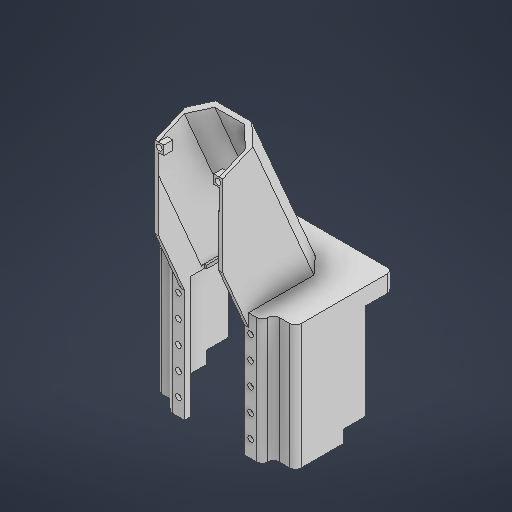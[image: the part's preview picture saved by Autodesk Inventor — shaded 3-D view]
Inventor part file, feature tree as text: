
AUTODESK INVENTOR PART (.ipt)
format: ipt  version: 2025 (Build 290162000, 162)  size: 475,136 bytes
history: native  units: in
note: dims shown in document units (in); Inventor stores cm internally (conversion verified against a paired STEP export)
features: extrude x10, sketch x10, chamfer x2, fillet x1, plane x1
ambient origin geometry x8: Origin, YZ Plane, XZ Plane, XY Plane, X Axis, Y Axis, Z Axis, Center Point
bodies: Solid1 (feature_tree)
feature tree (24):
  extrude  "Extrusion1"  Depth=0.1181in
  extrude  "Extrusion2"  Depth=0.0787in
  extrude  "Extrusion3"  Depth=1.9685in
  fillet  "Fillet1"  Radius=0.9843in
  chamfer  "Chamfer1"  Distance=0.4724in
  plane  "Work Plane1"
  extrude  "Extrusion4"  Depth=0.2165in
  chamfer  "Chamfer3"  Distance=0.1378in Angle=45.0deg
  extrude  "Extrusion7"  Depth=0.0787in
  extrude  "Extrusion8"  Depth=0.0787in
  extrude  "Extrusion9"  Depth=1.9685in
  sketch  "Sketch11"  dims[d23=0.1181in]
  extrude  "Extrusion10"  Depth=0.5906in
  sketch  "Sketch12"  dims[d27=0.1969in d28=0.1378in d29=0.0787in d30=45.0deg d31=0.0787in d32=0.0787in d33=1.9685in d34=0.5906in d36=2.126in d38=0.1575in d39=2.2835in d40=0.1378in d41=2.3622in d42=4.4705in d43=2.1969in d44=0.0in d45=0.0in d47=0.1575in d53=0.5512in d54=0.0787in d55=45.0deg d57=0.1181in d65=0.315in d67=0.3937in d69=0.6201in d70=0.3937in d71=0.7579in d72=0.315in d73=0.1598in d76=0.0787in d77=0.0787in d78=0.7579in d79=0.7579in d80=0.9843in d81=2.0472in d82=5.9055in d83=5.1186in d84=0.0in d85=0.6201in d86=0.7579in d90=3.7598in d91=0.0in d92=1.9685in d93=0.7874in d94=0.4331in d95=0.0in d96=0.315in d97=0.315in d98=0.0in d99=0.315in d100=0.0in d101=90.0deg d102=0.1969in d103=0.5906in d104=1.9685in d106=0.7874in d107=0.3937in d109=0.3937in d111=0.1969in d112=0.1575in d113=0.0in d114=0.1181in d115=0.0in d116=4.3504in]
  extrude  "Extrusion11"  Depth=2.126in
  extrude  "Extrusion12"  Depth=0.1575in
  sketch  "Sketch1"  dims[d1=2.9577in d2=0.1181in]
  sketch  "Sketch2"  dims[d8=4.2323in d9=0.0in d10=1.9685in d11=0.9843in]
  sketch  "Sketch3"  dims[d12=0.9449in]
  sketch  "Sketch4"  dims[d13=0.2165in]
  sketch  "Sketch8"  dims[d15=90.0deg d17=0.4724in d18=0.0in]
  sketch  "Sketch9"  dims[d19=0.1969in d20=0.2165in]
  sketch  "Sketch10"  dims[d22=0.1181in]
  sketch  "Sketch Rectangular Pattern1"  dims[d4=0.1181in d5=0.0in d6=0.0787in]
